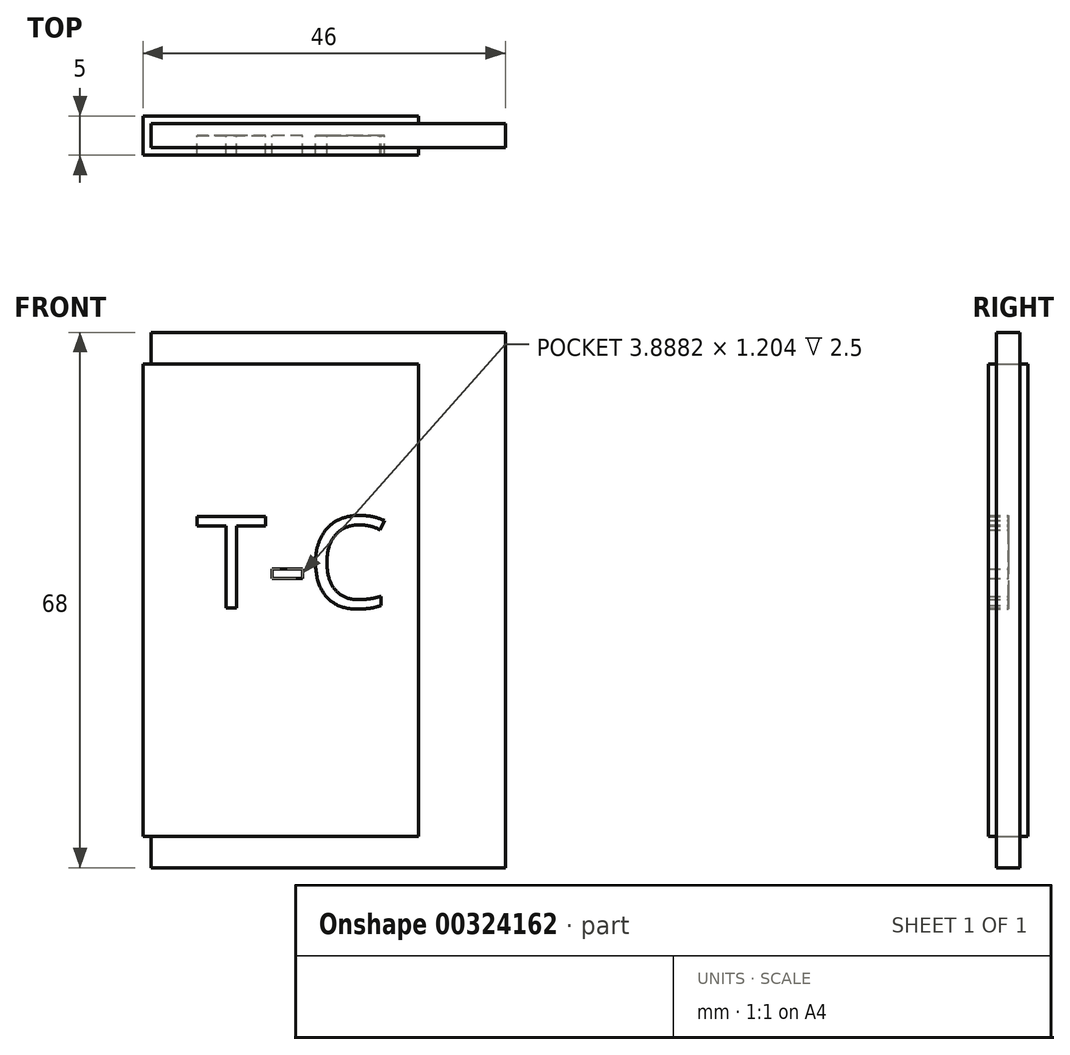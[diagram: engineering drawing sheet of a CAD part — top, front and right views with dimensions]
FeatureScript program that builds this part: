
annotation { "Feature Type Name" : "Feature", "Feature Type Description" : "" }
export const myFeature = defineFeature(function(context is Context, id is Id, definition is map)
    precondition{}
    {
        {
            var Q0;
            Q0=qCreatedBy(makeId("Front.planeOp"),FACE);
            var sketch = newSketch(context, id + "F0", { "sketchPlane" : qUnion([Q0])});
            skLineSegment(sketch, "E0.bottom", {"start": v(35.98, 19.78) * mm, "end": v(80.98, 19.78) * mm});
            skLineSegment(sketch, "E0.top", {"start": v(35.98, -48.22) * mm, "end": v(80.98, -48.22) * mm});
            skLineSegment(sketch, "E0.left", {"start": v(34.98, 15.78) * mm, "end": v(34.98, -44.22) * mm});
            skLineSegment(sketch, "E0.right", {"start": v(80.98, 19.78) * mm, "end": v(80.98, -48.22) * mm});
            skLineSegment(sketch, "E1.0", {"start": v(35.98, 19.78) * mm, "end": v(35.98, 15.78) * mm});
            skLineSegment(sketch, "E2.0", {"start": v(34.98, 15.78) * mm, "end": v(69.98, 15.78) * mm});
            skLineSegment(sketch, "E3.0", {"start": v(34.98, -44.22) * mm, "end": v(69.98, -44.22) * mm});
            skLineSegment(sketch, "E4.0", {"start": v(69.98, 15.78) * mm, "end": v(69.98, -44.22) * mm});
            skLineSegment(sketch, "E5.trimOffspring", {"start": v(35.98, -44.22) * mm, "end": v(35.98, -48.22) * mm});
            skText(sketch, "E6", { "text": "T-C", "fontName": "OpenSans-Regular.ttf"});
            const initialGuessF0  = {"E6": [0.0417, -0.01522, 1, 0, 0.01168]};
            skSetInitialGuess(sketch, initialGuessF0);
            skSolve(sketch);
        }
        {
            var Q0;
            Q0=makeQuery(id+"F0.imprint","IMPRINT",FACE,{"disambiguationData":[TD([[makeQuery(id+"F0.imprint","IMPRINT",EDGE,{"derivedFrom":sQuery(id+"F0.wireOp",EDGE,"E0.bottom")}),-1.0]])]});
            extrude(context, id + "F1", {"entities" : qUnion([Q0]), "endBound" : BoundingType.SYMMETRIC, "depth" : 3 * mm});
        }
        {
            var Q0;
            {var subQ3=sQuery(id+"F0.wireOp",EDGE,"E0.left");Q0=makeQuery(id+"F0.imprint","IMPRINT",FACE,{"disambiguationData":[TD([[makeQuery(id+"F0.imprint","IMPRINT",EDGE,{"derivedFrom":subQ3}),1.0]])]});}
            extrude(context, id + "F2", {"entities" : qUnion([Q0]), "operationType" : NewBodyOperationType.ADD, "endBound" : BoundingType.SYMMETRIC, "depth" : 5 * mm});
        }
        {
            var Q0;
            Q0=makeQuery(id+"F0.imprint","IMPRINT",FACE,{"disambiguationData":[TD([[makeQuery(id+"F0.imprint","IMPRINT",EDGE,{"derivedFrom":sQuery(id+"F0.wireOp",EDGE,"E6.sketch_text.stroke-0")}),-1.0]])]});
            var Q1;
            Q1=makeQuery(id+"F0.imprint","IMPRINT",FACE,{"disambiguationData":[TD([[makeQuery(id+"F0.imprint","IMPRINT",EDGE,{"derivedFrom":sQuery(id+"F0.wireOp",EDGE,"E6.sketch_text.stroke-8")}),-1.0]])]});
            var Q2;
            Q2=makeQuery(id+"F0.imprint","IMPRINT",FACE,{"disambiguationData":[TD([[makeQuery(id+"F0.imprint","IMPRINT",EDGE,{"derivedFrom":sQuery(id+"F0.wireOp",EDGE,"E6.sketch_text.stroke-12")}),-1.0]])]});
            extrude(context, id + "F3", {"entities" : qUnion([Q0, Q1, Q2]), "operationType" : NewBodyOperationType.ADD, "oppositeDirection" : true, "depth" : 2.5 * mm});
        }
    });
